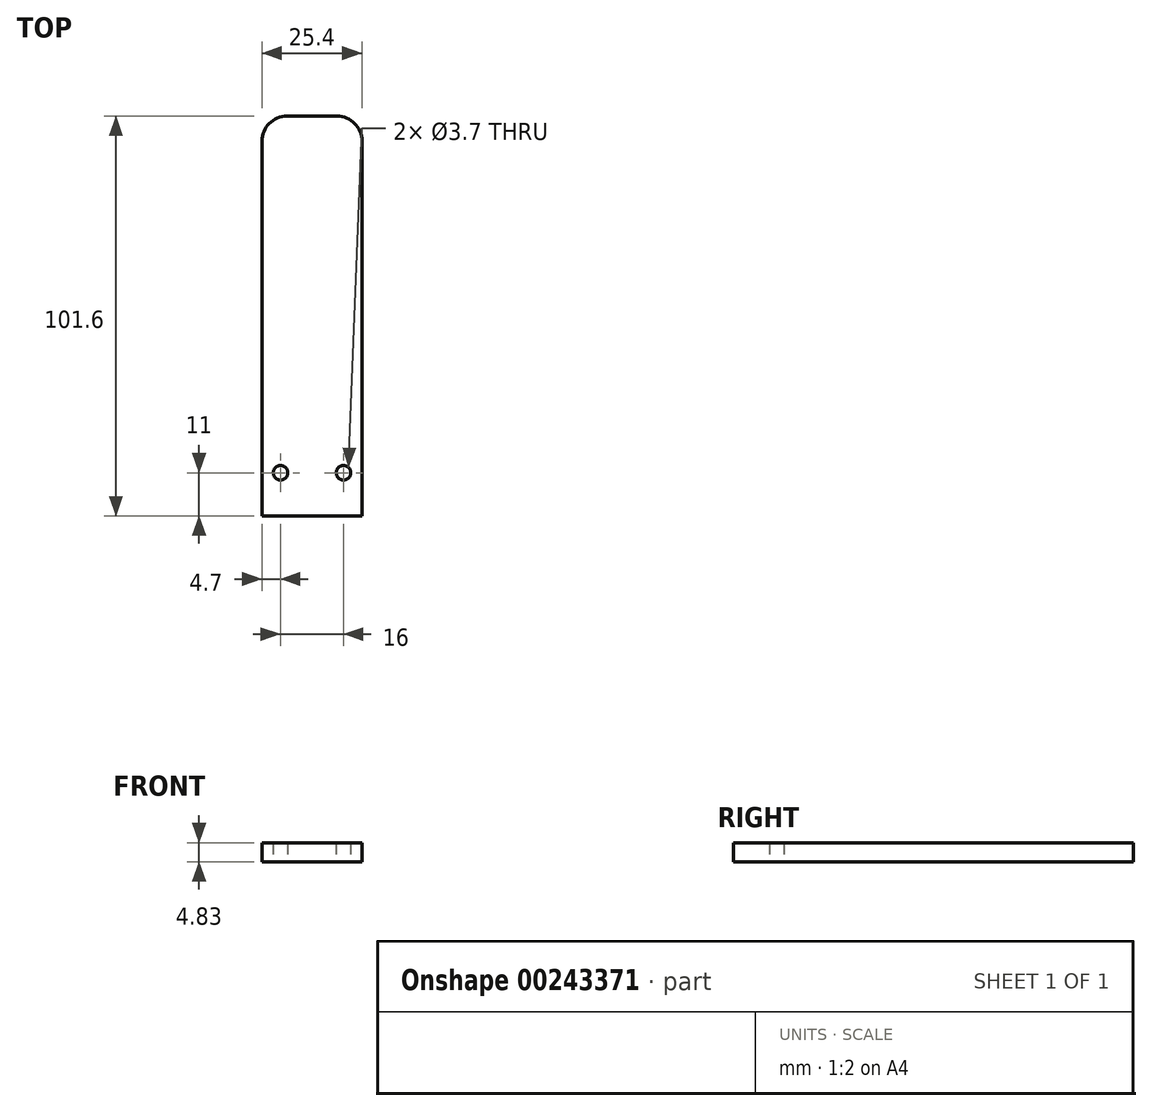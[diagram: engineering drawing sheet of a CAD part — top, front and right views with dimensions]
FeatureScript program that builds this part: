
annotation { "Feature Type Name" : "Feature", "Feature Type Description" : "" }
export const myFeature = defineFeature(function(context is Context, id is Id, definition is map)
    precondition{}
    {
        {
            var Q0;
            Q0=qCreatedBy(makeId("Top.planeOp"),FACE);
            var sketch = newSketch(context, id + "F0", { "sketchPlane" : qUnion([Q0])});
            skLineSegment(sketch, "E0.bottom", {"start": v(-6.35, 50.8) * mm, "end": v(6.35, 50.8) * mm});
            skLineSegment(sketch, "E0.top", {"start": v(-12.7, -50.8) * mm, "end": v(12.7, -50.8) * mm});
            skLineSegment(sketch, "E0.left", {"start": v(-12.7, 44.45) * mm, "end": v(-12.7, -50.8) * mm});
            skLineSegment(sketch, "E0.right", {"start": v(12.7, 44.45) * mm, "end": v(12.7, -50.8) * mm});
            skPoint(sketch, "E0.middle", {"position": v(0, 0) * mm});
            skLineSegment(sketch, "E1", {"start": v(0, -31.8) * mm, "end": v(0, -47.8) * mm, "construction": true});
            skLineSegment(sketch, "E2", {"start": v(0, -39.8) * mm, "end": v(12.7, -39.8) * mm, "construction": true});
            skCircle(sketch, "E3", {"center": v(8, -39.8) * mm, "radius": 1.85 * mm});
            skCircle(sketch, "E4.MirrorC", {"center": v(-8, -39.8) * mm, "radius": 1.85 * mm});
            skFitSpline(sketch, "E5", {"points": [v(0, 50.8) * mm, v(-12.7, -50.8) * mm], "startDerivative": vector(-38.1, 0) * mm, "endDerivative": vector(0, -115.34) * mm});
            skFitSpline(sketch, "E6.MirrorCS", {"points": [v(0, 50.8) * mm, v(12.7, -50.8) * mm], "startDerivative": vector(38.1, 0) * mm, "endDerivative": vector(0, -115.34) * mm});
            skArc(sketch, "E7.filletArc", {"start": v(-6.35, 50.8) * mm, "mid": v(-10.84, 48.94) * mm, "end": v(-12.7, 44.45) * mm});
            skArc(sketch, "E8.filletArc", {"start": v(12.7, 44.45) * mm, "mid": v(10.84, 48.94) * mm, "end": v(6.35, 50.8) * mm});
            skSolve(sketch);
        }
        {
            var Q0;
            Q0 = qSketchRegion(id + "F0", true);
            extrude(context, id + "F1", {"entities" : qUnion([Q0]), "depth" : 4.83 * mm});
        }
    });
